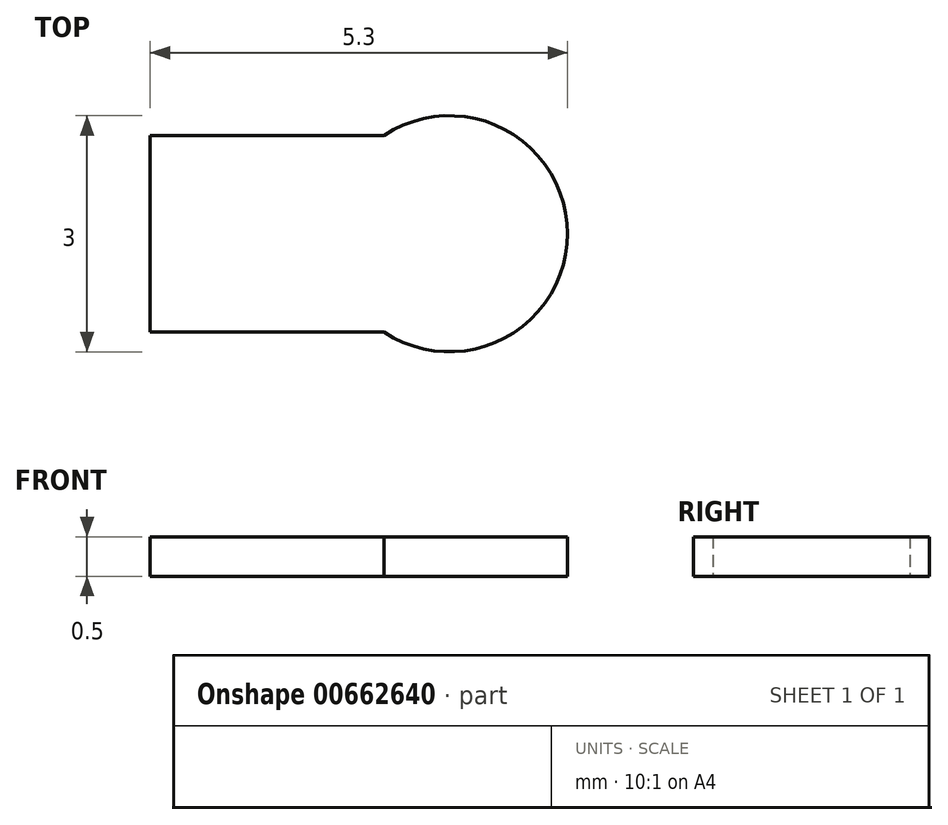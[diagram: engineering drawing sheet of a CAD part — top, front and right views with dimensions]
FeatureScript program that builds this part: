
annotation { "Feature Type Name" : "Feature", "Feature Type Description" : "" }
export const myFeature = defineFeature(function(context is Context, id is Id, definition is map)
    precondition{}
    {
        {
            var Q0;
            Q0=qCreatedBy(makeId("Top.planeOp"),FACE);
            var sketch = newSketch(context, id + "F0", { "sketchPlane" : qUnion([Q0])});
            skArc(sketch, "E0", {"start": v(-0.83, -1.25) * mm, "mid": v(1.5, 0) * mm, "end": v(-0.83, 1.25) * mm});
            skLineSegment(sketch, "E1", {"start": v(-0.83, 1.25) * mm, "end": v(-3.8, 1.25) * mm});
            skLineSegment(sketch, "E2", {"start": v(-3.8, 1.25) * mm, "end": v(-3.8, -1.25) * mm});
            skLineSegment(sketch, "E3", {"start": v(-3.8, -1.25) * mm, "end": v(-0.83, -1.25) * mm});
            skSolve(sketch);
        }
        {
            var Q0;
            Q0=makeQuery(id+"F0.imprint","IMPRINT",FACE,{"disambiguationData":[TD([[makeQuery(id+"F0.imprint","IMPRINT",EDGE,{"derivedFrom":sQuery(id+"F0.wireOp",EDGE,"E0")}),1.0]])]});
            extrude(context, id + "F1", {"entities" : qUnion([Q0]), "depth" : .5 * mm, "offsetDistance" : 25 * mm});
        }
    });
